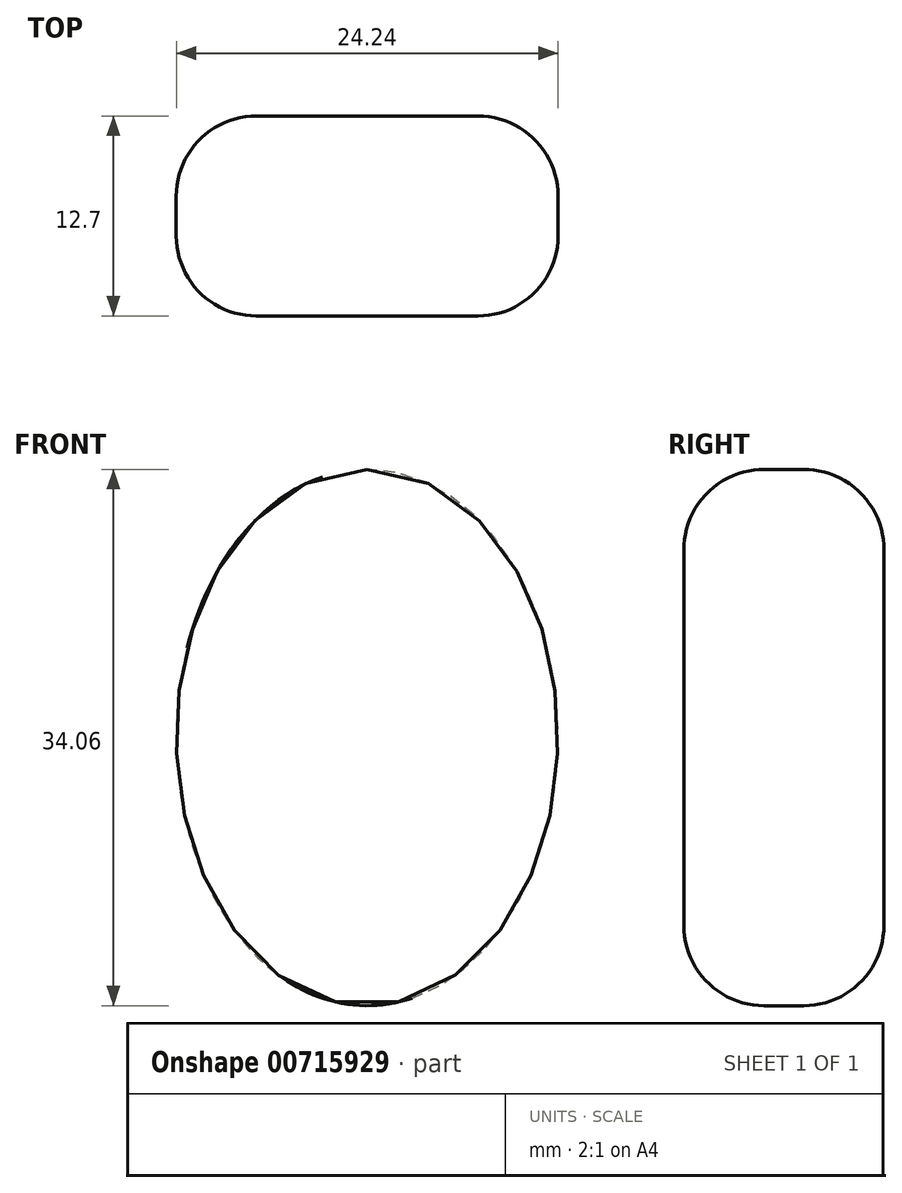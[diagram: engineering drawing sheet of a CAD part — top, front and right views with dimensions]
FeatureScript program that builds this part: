
annotation { "Feature Type Name" : "Feature", "Feature Type Description" : "" }
export const myFeature = defineFeature(function(context is Context, id is Id, definition is map)
    precondition{}
    {
        {
            var Q0;
            Q0=qCreatedBy(makeId("Front.planeOp"),FACE);
            var sketch = newSketch(context, id + "F0", { "sketchPlane" : qUnion([Q0])});
            skEllipse(sketch, "E0", {"center": v(0, 0) * mm, "majorRadius": 17.03 * mm, "minorRadius": 12.12 * mm, "majorAxis": v(0, 1)});
            skSolve(sketch);
        }
        {
            var Q0;
            Q0=makeQuery(id+"F0.imprint","IMPRINT",FACE,{"disambiguationData":[TD([[makeQuery(id+"F0.imprint","IMPRINT",EDGE,{"derivedFrom":sQuery(id+"F0.wireOp",EDGE,"E0")}),1.0]])]});
            extrude(context, id + "F1", {"entities" : qUnion([Q0]), "depth" : 12.7 * mm, "offsetDistance" : 25.4 * mm});
        }
        {
            var Q0;
            Q0=makeQuery(id+"F1.opExtrude","CAP_EDGE",EDGE,{"disambiguationData":[OSD([sQuery(id+"F0.wireOp",EDGE,"E0")])],"isStart":false});
            var Q1;
            Q1=makeQuery(id+"F1.opExtrude","CAP_EDGE",EDGE,{"disambiguationData":[OSD([sQuery(id+"F0.wireOp",EDGE,"E0")])],"isStart":true});
            fillet(context, id + "F2", {"entities" : qUnion([Q0, Q1]), "radius" : 5.08 * mm, "tangentPropagation" : true, "allowEdgeOverflow" : false});
        }
    });
